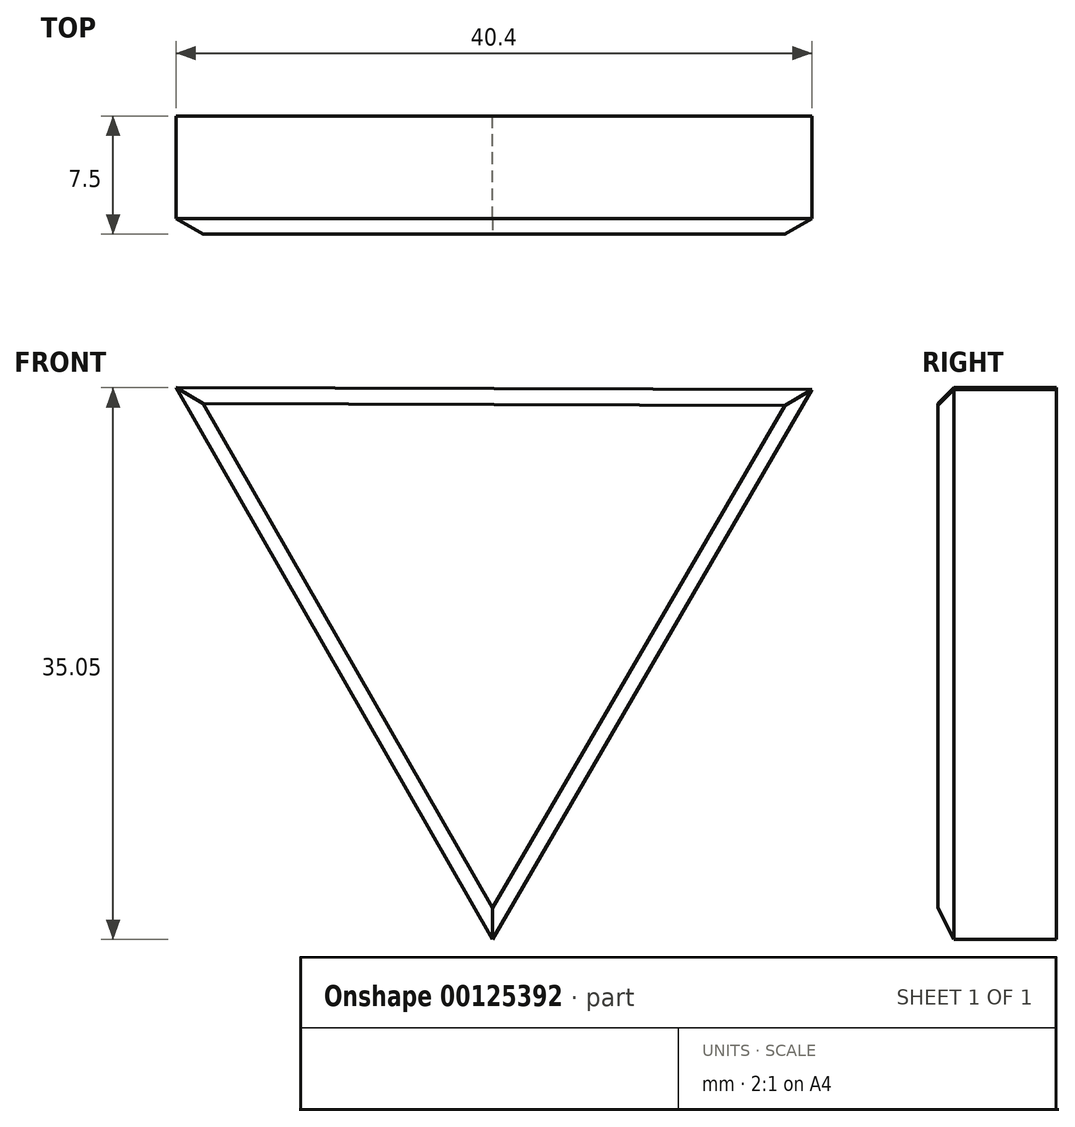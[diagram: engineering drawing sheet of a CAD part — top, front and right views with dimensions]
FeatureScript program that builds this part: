
annotation { "Feature Type Name" : "Feature", "Feature Type Description" : "" }
export const myFeature = defineFeature(function(context is Context, id is Id, definition is map)
    precondition{}
    {
        {
            var Q0;
            Q0=qCreatedBy(makeId("Front.planeOp"),FACE);
            var sketch = newSketch(context, id + "F0", { "sketchPlane" : qUnion([Q0])});
            skCircle(sketch, "E0.cCircle", {"center": v(0, 0) * mm, "radius": 23.32 * mm, "construction": true});
            skLineSegment(sketch, "E0.0", {"start": v(40.47, 23.2) * mm, "end": v(-0.15, -46.65) * mm});
            skLineSegment(sketch, "E0.1", {"start": v(-0.15, -46.65) * mm, "end": v(-40.32, 23.45) * mm});
            skLineSegment(sketch, "E0.2", {"start": v(-40.32, 23.45) * mm, "end": v(40.47, 23.2) * mm});
            skPoint(sketch, "E0.0.midPoint", {"position": v(20.16, -11.73) * mm});
            skSolve(sketch);
        }
        {
            var Q0;
            Q0=makeQuery(id+"F0.imprint","IMPRINT",FACE,{"disambiguationData":[TD([[makeQuery(id+"F0.imprint","IMPRINT",EDGE,{"derivedFrom":sQuery(id+"F0.wireOp",EDGE,"E0.0")}),-1.0]])]});
            extrude(context, id + "F1", {"entities" : qUnion([Q0]), "depth" : 15 * mm});
        }
        {
            var Q0;
            Q0=makeQuery(id+"F1.opExtrude","CAP_EDGE",EDGE,{"disambiguationData":[OSD([sQuery(id+"F0.wireOp",EDGE,"E0.2")])],"isStart":false});
            var Q1;
            Q1=makeQuery(id+"F1.opExtrude","CAP_FACE",FACE,{"disambiguationData":[OSD([sQuery(id+"F0.wireOp",EDGE,"E0.0"),sQuery(id+"F0.wireOp",EDGE,"E0.1"),sQuery(id+"F0.wireOp",EDGE,"E0.2")])],"isStart":false});
            chamfer(context, id + "F2", {"entities" : qUnion([Q0, Q1]), "width" : 2 * mm, "tangentPropagation" : true});
        }
        {
            var Q0;
            Q0=makeQuery(id+"F1.opExtrude","SWEPT_BODY",BODY,{"disambiguationData":[OSD([sQuery(id+"F0.wireOp",EDGE,"E0.0"),sQuery(id+"F0.wireOp",EDGE,"E0.1"),sQuery(id+"F0.wireOp",EDGE,"E0.2")])]});
            var Q1;
            Q1=qCreatedBy(makeId("Origin.pointOp"),VERTEX);
            transform(context, id + "F3", {"entities" : qUnion([Q0]), "transformType" : TransformType.SCALE_UNIFORMLY, "scale" : .5, "scalePoint" : qUnion([Q1]), "makeCopy" : false});
        }
    });
